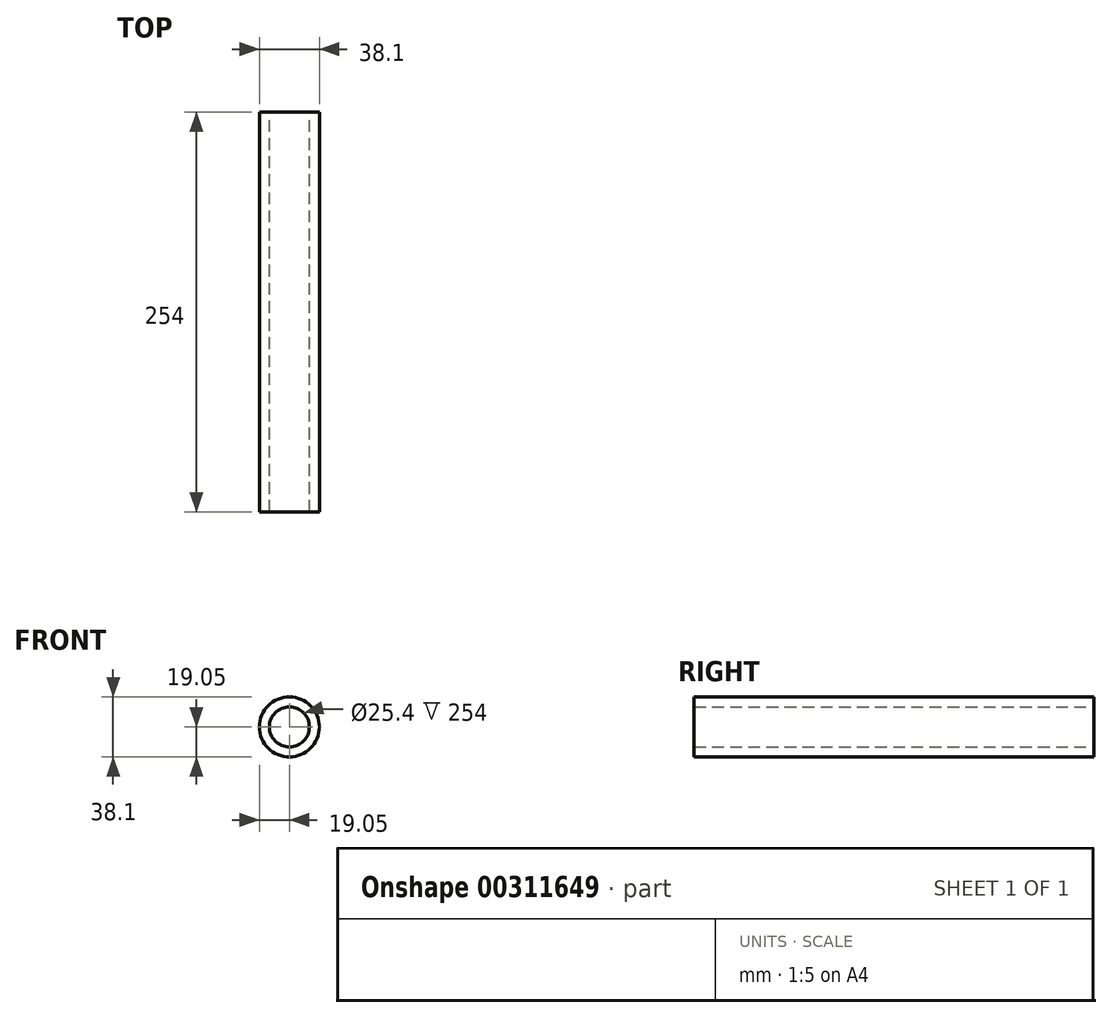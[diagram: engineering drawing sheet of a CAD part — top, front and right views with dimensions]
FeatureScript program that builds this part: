
annotation { "Feature Type Name" : "Feature", "Feature Type Description" : "" }
export const myFeature = defineFeature(function(context is Context, id is Id, definition is map)
    precondition{}
    {
        {
            var Q0;
            Q0=qCreatedBy(makeId("Front.planeOp"),FACE);
            var sketch = newSketch(context, id + "F0", { "sketchPlane" : qUnion([Q0])});
            skCircle(sketch, "E0", {"center": v(0, 0) * mm, "radius": 12.7 * mm});
            skCircle(sketch, "E1", {"center": v(0, 0) * mm, "radius": 19.05 * mm});
            skSolve(sketch);
        }
        {
            var Q0;
            Q0 = qSketchRegion(id + "F0", true);
            extrude(context, id + "F1", {"entities" : qUnion([Q0]), "depth" : 254 * mm});
        }
    });
